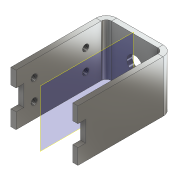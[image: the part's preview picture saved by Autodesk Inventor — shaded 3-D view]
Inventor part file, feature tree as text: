
AUTODESK INVENTOR PART (.ipt)
format: ipt  version: 2018.1 (Build 221171000, 171)  size: 166,912 bytes
history: native  units: mm
features: other x7, hole x4, sketch x2, imported_body x1, mirror x1
ambient origin geometry x8: Origin, YZ Plane, XZ Plane, XY Plane, X Axis, Y Axis, Z Axis, Center Point
bodies: Body1 (feature_tree)
feature tree (15):
  imported_body  "base"
  other  "Твердое тело1"
  other  "Грань1"
  other  "Грань3"
  other  "РабПлоскость3"
  mirror  "Зеркальное отражение2"
  hole  "Отверстие1"  [1 undecoded]
  hole  "Отверстие2"  [1 undecoded]
  hole  "Отверстие3"  [1 undecoded]
  hole  "Отверстие4"  [1 undecoded]
  sketch  "Эскиз1"
  other  "Пластина1"
  sketch  "Эскиз2"
  other  "Пластина3"
  other  "Сгиб2"
note: 4 required parameter values undecoded (feature->parameter linkage not recoverable at this tier; creation-order binding heuristic only, values carry confidence <= 0.55)
